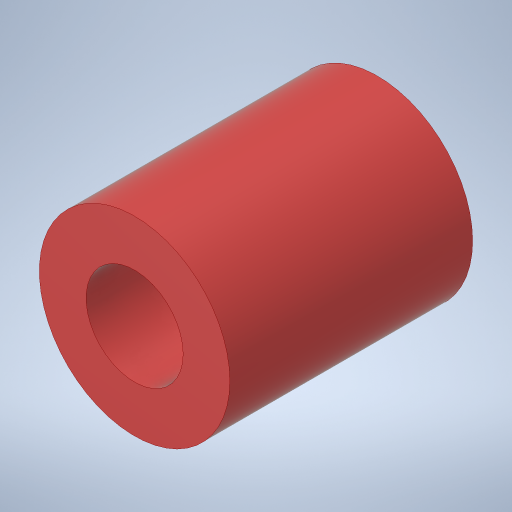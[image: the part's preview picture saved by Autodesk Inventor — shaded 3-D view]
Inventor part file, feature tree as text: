
AUTODESK INVENTOR PART (.ipt)
format: ipt  version: 2023.4 (Build 274418000, 418)  size: 236,032 bytes
history: native  units: in
note: dims shown in document units (in); Inventor stores cm internally (conversion verified against a paired STEP export)
features: extrude x1
ambient origin geometry x8: Origin, YZ Plane, XZ Plane, XY Plane, X Axis, Y Axis, Z Axis, Center Point
bodies: Solid1 (feature_tree)
feature tree (1):
  extrude  "Extrusion1"  TaperAngle=0.0deg  [1 undecoded]
note: 1 required parameter value undecoded (feature->parameter linkage not recoverable at this tier; creation-order binding heuristic only, values carry confidence <= 0.55)
